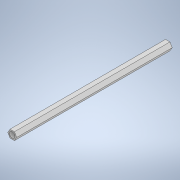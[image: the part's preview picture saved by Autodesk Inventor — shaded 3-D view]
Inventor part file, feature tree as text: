
AUTODESK INVENTOR PART (.ipt)
format: ipt  version: 2022.2 (Build 262287010, 287A)  size: 116,224 bytes
history: native  units: in
note: dims shown in document units (in); Inventor stores cm internally (conversion verified against a paired STEP export)
features: sketch x3, hole x2, extrude x1
ambient origin geometry x8: Origin, YZ Plane, XZ Plane, XY Plane, X Axis, Y Axis, Z Axis, Center Point
bodies: Body1 (feature_tree)
feature tree (6):
  extrude  "Extrusion2"  Depth=0.375in
  hole  "Hole1"  [1 undecoded]
  hole  "Hole2"  [1 undecoded]
  sketch  "Sketch1"  dims[d0=0.375in d3=0.159in]
  sketch  "Sketch2"  dims[d4=7.5625in d5=0.0in]
  sketch  "Sketch3"  dims[d6=0.24in d7=0.75in d8=0.27in d9=0.2411in d10=0.5635in d11=0.31in d12=0.0in d13=0.24in d14=0.75in d15=0.27in d16=0.2411in d17=0.5635in d18=0.31in d19=0.0in]
note: 2 required parameter values undecoded (feature->parameter linkage not recoverable at this tier; creation-order binding heuristic only, values carry confidence <= 0.55)
